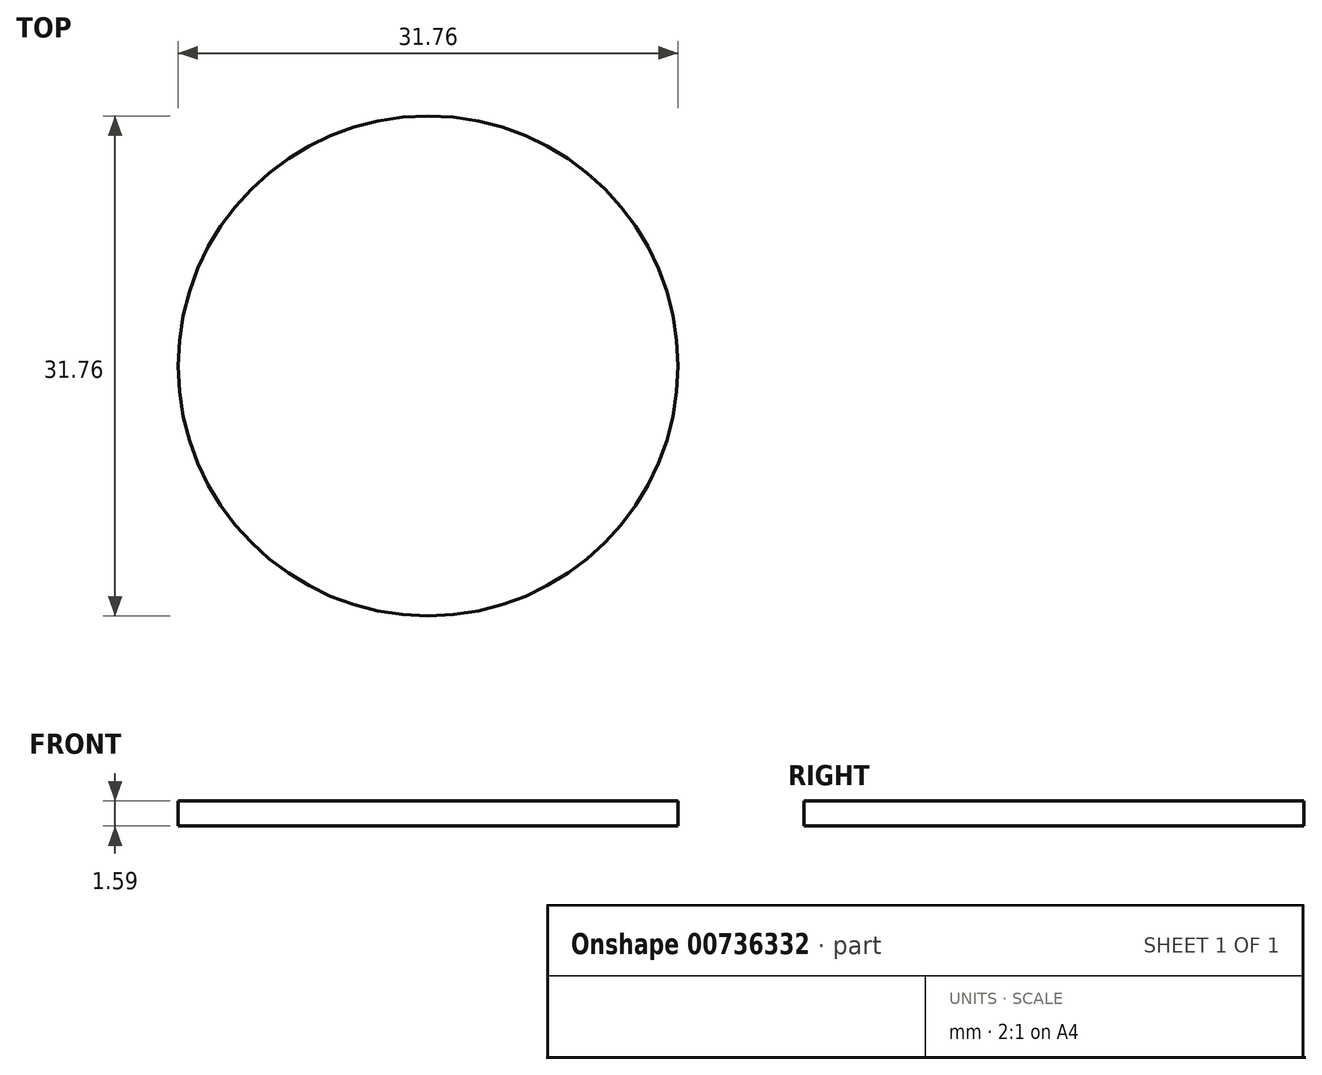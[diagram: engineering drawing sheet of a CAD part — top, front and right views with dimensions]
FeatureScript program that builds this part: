
annotation { "Feature Type Name" : "Feature", "Feature Type Description" : "" }
export const myFeature = defineFeature(function(context is Context, id is Id, definition is map)
    precondition{}
    {
        {
            var Q0;
            Q0=qCreatedBy(makeId("Top.planeOp"),FACE);
            var sketch = newSketch(context, id + "F0", { "sketchPlane" : qUnion([Q0])});
            skCircle(sketch, "E0", {"center": v(0, 0) * mm, "radius": 15.88 * mm});
            skSolve(sketch);
        }
        {
            var Q0;
            Q0 = qSketchRegion(id + "F0", true);
            extrude(context, id + "F1", {"entities" : qUnion([Q0]), "depth" : 1.59 * mm, "offsetDistance" : 25.4 * mm});
        }
    });
